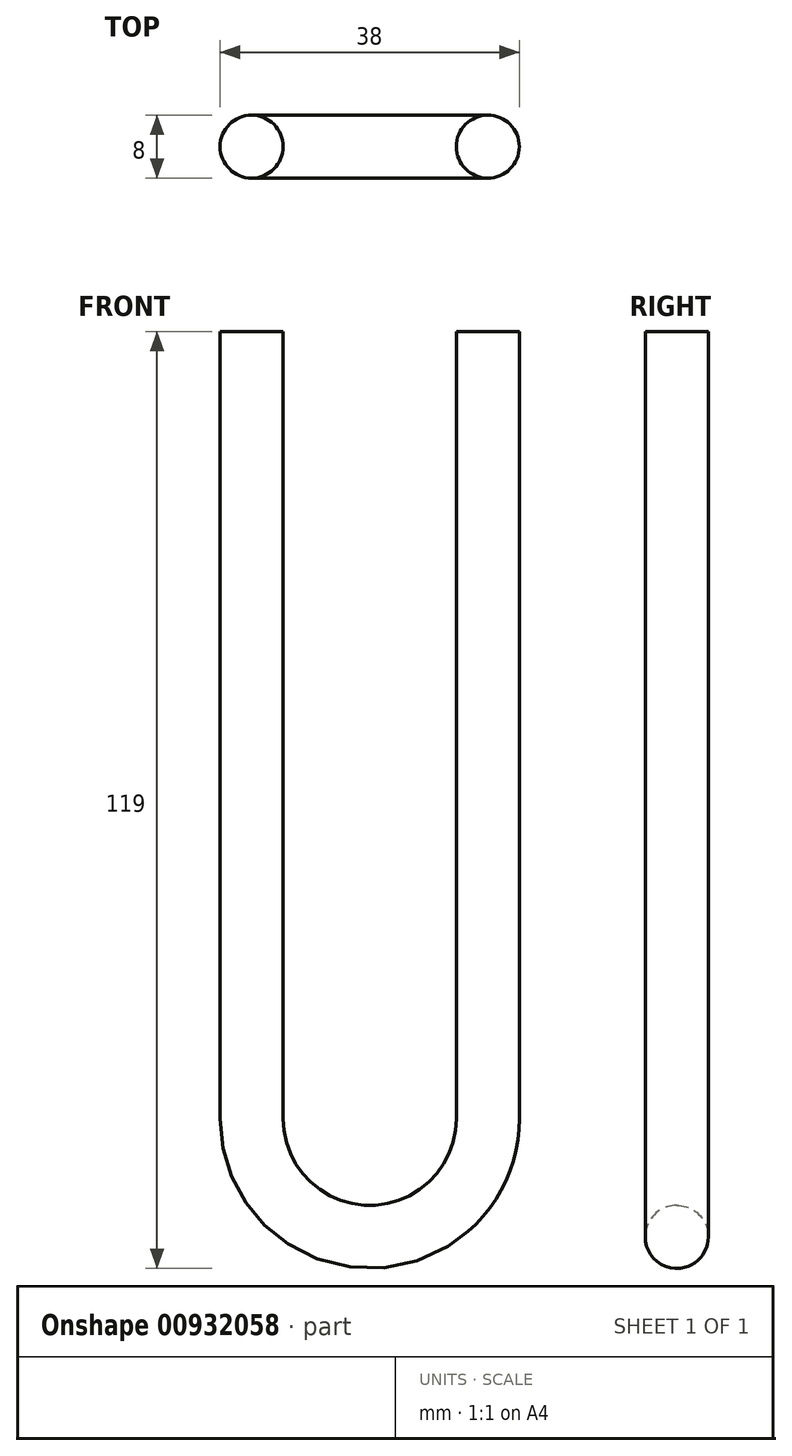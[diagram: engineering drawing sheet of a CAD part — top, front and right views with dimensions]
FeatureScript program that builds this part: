
annotation { "Feature Type Name" : "Feature", "Feature Type Description" : "" }
export const myFeature = defineFeature(function(context is Context, id is Id, definition is map)
    precondition{}
    {
        {
            var Q0;
            Q0=qCreatedBy(makeId("Front.planeOp"),FACE);
            var sketch = newSketch(context, id + "F0", { "sketchPlane" : qUnion([Q0])});
            skLineSegment(sketch, "E0", {"start": v(0, 0) * mm, "end": v(0, 100) * mm});
            skLineSegment(sketch, "E1", {"start": v(30, 100) * mm, "end": v(30, 0) * mm});
            skArc(sketch, "E2", {"start": v(0, 0) * mm, "mid": v(15, -15) * mm, "end": v(30, 0) * mm});
            skSolve(sketch);
        }
        {
            var Q0;
            Q0=qCreatedBy(makeId("Top.planeOp"),FACE);
            var sketch = newSketch(context, id + "F1", { "sketchPlane" : qUnion([Q0])});
            skCircle(sketch, "E3", {"center": v(0, 0) * mm, "radius": 4 * mm});
            skSolve(sketch);
        }
        {
            var Q0;
            Q0=makeQuery(id+"F1.imprint","IMPRINT",FACE,{"disambiguationData":[TD([[makeQuery(id+"F1.imprint","IMPRINT",EDGE,{"derivedFrom":sQuery(id+"F1.wireOp",EDGE,"E3")}),1.0]])]});
            var Q1;
            Q1=sQuery(id+"F0.wireOp",EDGE,"E0");
            var Q2;
            Q2=sQuery(id+"F0.wireOp",EDGE,"E1");
            var Q3;
            Q3=sQuery(id+"F0.wireOp",EDGE,"E2");
            sweep(context, id + "F2", {"profiles" : qUnion([Q0]), "path" : qUnion([Q1, Q2, Q3])});
        }
    });
